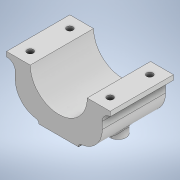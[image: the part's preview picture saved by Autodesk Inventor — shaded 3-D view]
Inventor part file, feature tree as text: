
AUTODESK INVENTOR PART (.ipt)
format: ipt  version: 2021 (Build 250183000, 183)  size: 298,496 bytes
history: native  units: mm
features: extrude x5, sketch x5, fillet x1, projected_geometry x1
ambient origin geometry x8: Origin, YZ Plane, XZ Plane, XY Plane, X Axis, Y Axis, Z Axis, Center Point
bodies: Solid1 (feature_tree)
feature tree (12):
  extrude  "Extrusion1"  Depth=55.0mm
  extrude  "Extrusion2"  Depth=3.0mm
  extrude  "Extrusion3"  Depth=5.0mm
  extrude  "Extrusion4"  TaperAngle=90.0deg  [1 undecoded]
  extrude  "Extrusion5"  Depth=2.0mm TaperAngle=0.0deg
  fillet  "Fillet1"  Radius=15.0mm
  sketch  "Sketch1"  dims[d0=36.0mm d1=55.0mm]
  sketch  "Sketch2"  dims[d2=15.0mm d3=3.0mm]
  sketch  "Sketch3"  dims[d4=5.0mm d5=5.0mm]
  sketch  "Sketch4"  dims[d6=3.0mm d7=90.0deg]
  sketch  "Sketch5"  dims[d8=5.0mm d9=40.0mm d10=0.0mm d11=15.0mm d12=10.0mm d13=10.0mm d14=5.0mm d15=0.0mm d16=4.8mm d17=4.8mm d18=15.0mm d19=0.0mm d20=4.0mm d21=7.5mm d22=7.5mm d23=20.0mm d25=50.5mm d26=20.0mm d28=25.0mm d31=10.0mm d32=0.0mm d33=2.0mm d34=0.0mm d35=2.0mm]
  projected_geometry  "Projected Loop1"
note: 1 required parameter value undecoded (feature->parameter linkage not recoverable at this tier; creation-order binding heuristic only, values carry confidence <= 0.55)
